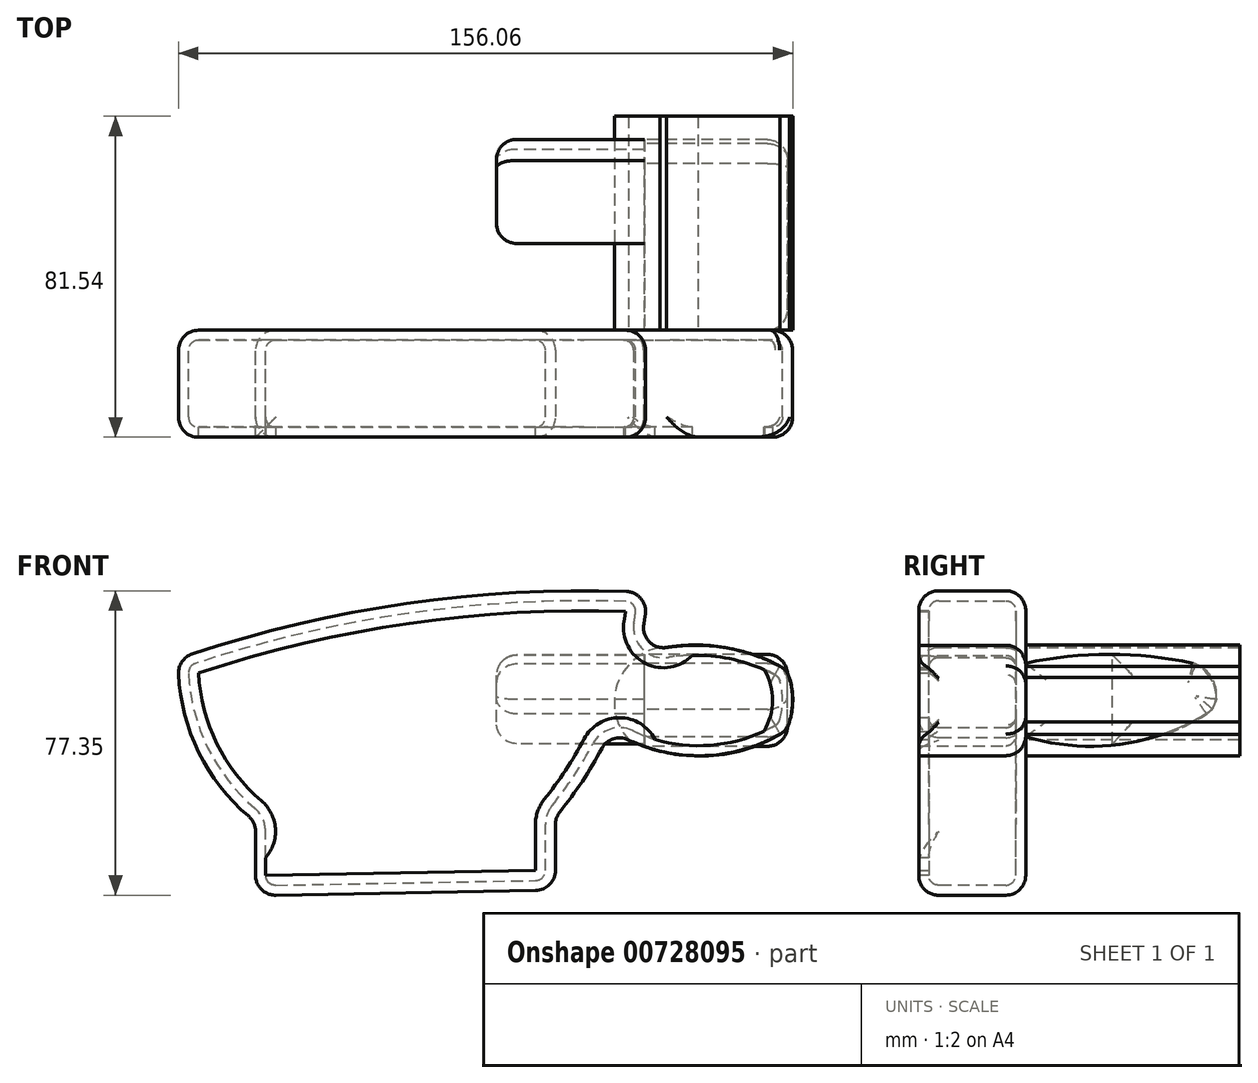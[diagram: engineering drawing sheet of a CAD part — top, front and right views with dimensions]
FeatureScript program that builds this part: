
annotation { "Feature Type Name" : "Feature", "Feature Type Description" : "" }
export const myFeature = defineFeature(function(context is Context, id is Id, definition is map)
    precondition{}
    {
        {
            var Q0;
            Q0=qCreatedBy(makeId("Front.planeOp"),FACE);
            var sketch = newSketch(context, id + "F0", { "sketchPlane" : qUnion([Q0])});
            skLineSegment(sketch, "E0", {"start": v(-61.22, -77.05) * mm, "end": v(-61.22, -58.3) * mm});
            skLineSegment(sketch, "E1", {"start": v(14.97, -75.67) * mm, "end": v(14.97, -57.2) * mm});
            skArc(sketch, "E2", {"start": v(-80.82, -16.86) * mm, "mid": v(-75.96, -39.92) * mm, "end": v(-61.22, -58.3) * mm});
            skLineSegment(sketch, "E3", {"start": v(-61.22, -77.05) * mm, "end": v(14.97, -75.67) * mm});
            skArc(sketch, "E4", {"start": v(38.47, 0) * mm, "mid": v(-21.98, -2.73) * mm, "end": v(-80.82, -16.86) * mm});
            skArc(sketch, "E5", {"start": v(14.97, -57.2) * mm, "mid": v(31.1, -30.4) * mm, "end": v(38.47, 0) * mm});
            skArc(sketch, "E6", {"start": v(73.75, -19.7) * mm, "mid": v(55.22, -13.68) * mm, "end": v(35.85, -15.83) * mm});
            skArc(sketch, "E7", {"start": v(73.75, -35.02) * mm, "mid": v(75.2, -27.36) * mm, "end": v(73.75, -19.7) * mm});
            skArc(sketch, "E8", {"start": v(29.06, -35.02) * mm, "mid": v(51.4, -41.51) * mm, "end": v(73.75, -35.02) * mm});
            skSolve(sketch);
        }
        {
            var Q0;
            Q0 = qSketchRegion(id + "F0", true);
            var Q1;
            Q1=makeQuery(id+"F0.imprint","IMPRINT",FACE,{"disambiguationData":[TD([[makeQuery(id+"F0.imprint","IMPRINT",EDGE,{"derivedFrom":sQuery(id+"F0.wireOp",EDGE,"E0")}),-1.0]])]});
            extrude(context, id + "F1", {"entities" : qUnion([Q0, Q1]), "depth" : 27.18 * mm, "offsetDistance" : 25.4 * mm});
        }
        {
            var Q0;
            Q0=makeQuery(id+"F1.opExtrude","SWEPT_FACE",FACE,{"disambiguationData":[OSD([sQuery(id+"F0.wireOp",EDGE,"E2")])]});
            var Q1;
            Q1=makeQuery(id+"F1.opExtrude","SWEPT_FACE",FACE,{"disambiguationData":[OSD([sQuery(id+"F0.wireOp",EDGE,"E4")])]});
            var Q2;
            Q2=makeQuery(id+"F1.opExtrude","SWEPT_FACE",FACE,{"disambiguationData":[OSD([sQuery(id+"F0.wireOp",EDGE,"80HTwHrn-uGDa-Itzb-pdZH-r85gItSOkt19")])]});
            var Q3;
            Q3=makeQuery(id+"F1.opExtrude","CAP_EDGE",EDGE,{"disambiguationData":[OSD([sQuery(id+"F0.wireOp",EDGE,"E3")])],"isStart":false});
            var Q4;
            Q4=makeQuery(id+"F1.opExtrude","SWEPT_FACE",FACE,{"disambiguationData":[OSD([sQuery(id+"F0.wireOp",EDGE,"E3")])]});
            var Q5;
            Q5=makeQuery(id+"F1.opExtrude","CAP_EDGE",EDGE,{"disambiguationData":[OSD([sQuery(id+"F0.wireOp",EDGE,"E5")])],"isStart":false});
            var Q6;
            Q6=makeQuery(id+"F1.opExtrude","SWEPT_FACE",FACE,{"disambiguationData":[OSD([sQuery(id+"F0.wireOp",EDGE,"E5")])]});
            var Q7;
            Q7=makeQuery(id+"F1.opExtrude","SWEPT_FACE",FACE,{"disambiguationData":[OSD([sQuery(id+"F0.wireOp",EDGE,"E1")])]});
            var Q8;
            Q8=makeQuery(id+"F1.opExtrude","CAP_FACE",FACE,{"disambiguationData":[OSD([sQuery(id+"F0.wireOp",EDGE,"E0"),sQuery(id+"F0.wireOp",EDGE,"E1"),sQuery(id+"F0.wireOp",EDGE,"E2"),sQuery(id+"F0.wireOp",EDGE,"E3"),sQuery(id+"F0.wireOp",EDGE,"E4"),sQuery(id+"F0.wireOp",EDGE,"E5"),sQuery(id+"F0.wireOp",EDGE,"E6"),sQuery(id+"F0.wireOp",EDGE,"E7"),sQuery(id+"F0.wireOp",EDGE,"E8")])],"isStart":true});
            fillet(context, id + "F2", {"entities" : qUnion([Q0, Q1, Q2, Q3, Q4, Q5, Q6, Q7, Q8]), "radius" : 5.08 * mm, "tangentPropagation" : true, "allowEdgeOverflow" : false});
        }
        {
            var Q0;
            Q0=qCreatedBy(makeId("Right.planeOp"),FACE);
            var sketch = newSketch(context, id + "F3", { "sketchPlane" : qUnion([Q0])});
            skArc(sketch, "E9", {"start": v(0, -36.7) * mm, "mid": v(0.07, -27.35) * mm, "end": v(0, -18) * mm});
            skArc(sketch, "E10", {"start": v(0, -36.7) * mm, "mid": v(24.5, -38.51) * mm, "end": v(47.43, -29.72) * mm});
            skArc(sketch, "E11", {"start": v(42.41, -18) * mm, "mid": v(21.2, -15.77) * mm, "end": v(0, -18) * mm});
            skArc(sketch, "E12", {"start": v(47.43, -29.72) * mm, "mid": v(47.8, -22.64) * mm, "end": v(42.41, -18) * mm});
            skSolve(sketch);
        }
        {
            var Q0;
            Q0=makeQuery(id+"F3.imprint","IMPRINT",FACE,{"disambiguationData":[TD([[makeQuery(id+"F3.imprint","IMPRINT",EDGE,{"derivedFrom":sQuery(id+"F3.wireOp",EDGE,"E9")}),-1.0]])]});
            var Q1;
            {var subQ0=sQuery(id+"F0.wireOp",EDGE,"E6");Q1=makeQuery(id+"F2.opFillet","BLEND_FACE",FACE,{"disambiguationData":[OSD([subQ0]),TDD([makeQuery(id+"F1.opExtrude","CAP_EDGE",EDGE,{"disambiguationData":[OSD([subQ0])],"isStart":true})])]});}
            extrude(context, id + "F4", {"entities" : qUnion([Q0]), "depth" : 73.9 * mm, "endBoundEntityFace" : qUnion([Q1]), "offsetDistance" : 25.4 * mm, "hasSecondDirection" : true, "secondDirectionOppositeDirection" : false, "secondDirectionDepth" : 37.6 * mm});
        }
        {
            var Q0;
            Q0=qCreatedBy(makeId("Right.planeOp"),FACE);
            var sketch = newSketch(context, id + "F5", { "sketchPlane" : qUnion([Q0])});
            skArc(sketch, "E13", {"start": v(48.5, -27.23) * mm, "mid": v(47.09, -21.98) * mm, "end": v(43.15, -18.23) * mm});
            skArc(sketch, "E14", {"start": v(45.97, -30.88) * mm, "mid": v(47.54, -29.27) * mm, "end": v(48.5, -27.23) * mm});
            skArc(sketch, "E15", {"start": v(22.07, -38.47) * mm, "mid": v(34.56, -36.37) * mm, "end": v(45.97, -30.88) * mm});
            skLineSegment(sketch, "E16", {"start": v(0, -25.25) * mm, "end": v(0, -17.01) * mm});
            skLineSegment(sketch, "E17", {"start": v(22.07, -20.7) * mm, "end": v(22.07, -38.47) * mm});
            skArc(sketch, "E18", {"start": v(43.15, -18.23) * mm, "mid": v(32.68, -16.44) * mm, "end": v(22.07, -15.98) * mm});
            skPoint(sketch, "E18.endSnap0", {"position": v(22.07, -29.58) * mm});
            skLineSegment(sketch, "E19", {"start": v(22.07, -20.7) * mm, "end": v(22.07, -15.98) * mm});
            skSolve(sketch);
        }
        {
            var Q0;
            Q0 = qSketchRegion(id + "F5", true);
            extrude(context, id + "F6", {"entities" : qUnion([Q0]), "operationType" : NewBodyOperationType.ADD, "depth" : 37.6 * mm, "offsetDistance" : 25.4 * mm});
        }
        {
            var Q0;
            Q0=makeQuery(id+"F6.opExtrude","CAP_FACE",FACE,{"disambiguationData":[OSD([sQuery(id+"F5.wireOp",EDGE,"E13"),sQuery(id+"F5.wireOp",EDGE,"E14"),sQuery(id+"F5.wireOp",EDGE,"E15"),sQuery(id+"F5.wireOp",EDGE,"E17"),sQuery(id+"F5.wireOp",EDGE,"E18"),sQuery(id+"F5.wireOp",EDGE,"E19")])],"isStart":true});
            var Q1;
            Q1=makeQuery(id+"F1.opExtrude","SWEPT_FACE",FACE,{"disambiguationData":[OSD([sQuery(id+"F0.wireOp",EDGE,"E7")])]});
            var Q2;
            Q2=makeQuery(id+"F4.opExtrude","CAP_FACE",FACE,{"disambiguationData":[OSD([sQuery(id+"F3.wireOp",EDGE,"E9"),sQuery(id+"F3.wireOp",EDGE,"E10"),sQuery(id+"F3.wireOp",EDGE,"E11"),sQuery(id+"F3.wireOp",EDGE,"E12")])],"isStart":false});
            fillet(context, id + "F7", {"entities" : qUnion([Q0, Q1, Q2]), "radius" : 5.08 * mm, "tangentPropagation" : true, "allowEdgeOverflow" : false});
        }
        {
            var Q0;
            Q0=makeQuery(id+"F1.opExtrude","CAP_FACE",FACE,{"disambiguationData":[OSD([sQuery(id+"F0.wireOp",EDGE,"E0"),sQuery(id+"F0.wireOp",EDGE,"E1"),sQuery(id+"F0.wireOp",EDGE,"E2"),sQuery(id+"F0.wireOp",EDGE,"E3"),sQuery(id+"F0.wireOp",EDGE,"E4"),sQuery(id+"F0.wireOp",EDGE,"E5"),sQuery(id+"F0.wireOp",EDGE,"E6"),sQuery(id+"F0.wireOp",EDGE,"E7"),sQuery(id+"F0.wireOp",EDGE,"E8")])],"isStart":false});
            shell(context, id + "F8", {"entities" : qUnion([Q0]), "thickness" : 2.54 * mm});
        }
        {
            var Q0;
            Q0=qCreatedBy(makeId("Front.planeOp"),FACE);
            var sketch = newSketch(context, id + "F9", { "sketchPlane" : qUnion([Q0])});
            skArc(sketch, "E20", {"start": v(41.5, -14.01) * mm, "mid": v(30.67, -23.43) * mm, "end": v(33.6, -37.49) * mm});
            skArc(sketch, "E21", {"start": v(33.6, -37.49) * mm, "mid": v(42.19, -40.53) * mm, "end": v(51.24, -41.54) * mm});
            skArc(sketch, "E22", {"start": v(51.24, -41.54) * mm, "mid": v(62, -40.29) * mm, "end": v(71.96, -36.07) * mm});
            skArc(sketch, "E23", {"start": v(71.96, -36.07) * mm, "mid": v(73.58, -34.81) * mm, "end": v(74.39, -32.94) * mm});
            skArc(sketch, "E24", {"start": v(74.39, -32.94) * mm, "mid": v(75.28, -27.3) * mm, "end": v(74.39, -21.68) * mm});
            skArc(sketch, "E25", {"start": v(74.39, -21.68) * mm, "mid": v(73.5, -19.95) * mm, "end": v(71.96, -18.78) * mm});
            skArc(sketch, "E26", {"start": v(71.96, -18.78) * mm, "mid": v(65.2, -15.82) * mm, "end": v(58.04, -14.01) * mm});
            skArc(sketch, "E27", {"start": v(58.04, -14.01) * mm, "mid": v(50.61, -13.39) * mm, "end": v(43.18, -14.01) * mm});
            skArc(sketch, "E28", {"start": v(41.5, -14.01) * mm, "mid": v(42.34, -14.08) * mm, "end": v(43.18, -14.01) * mm});
            skSolve(sketch);
        }
        {
            var Q0;
            Q0 = qSketchRegion(id + "F9", true);
            extrude(context, id + "F10", {"entities" : qUnion([Q0]), "oppositeDirection" : true, "depth" : 54.36 * mm, "offsetDistance" : 25.4 * mm});
        }
    });
